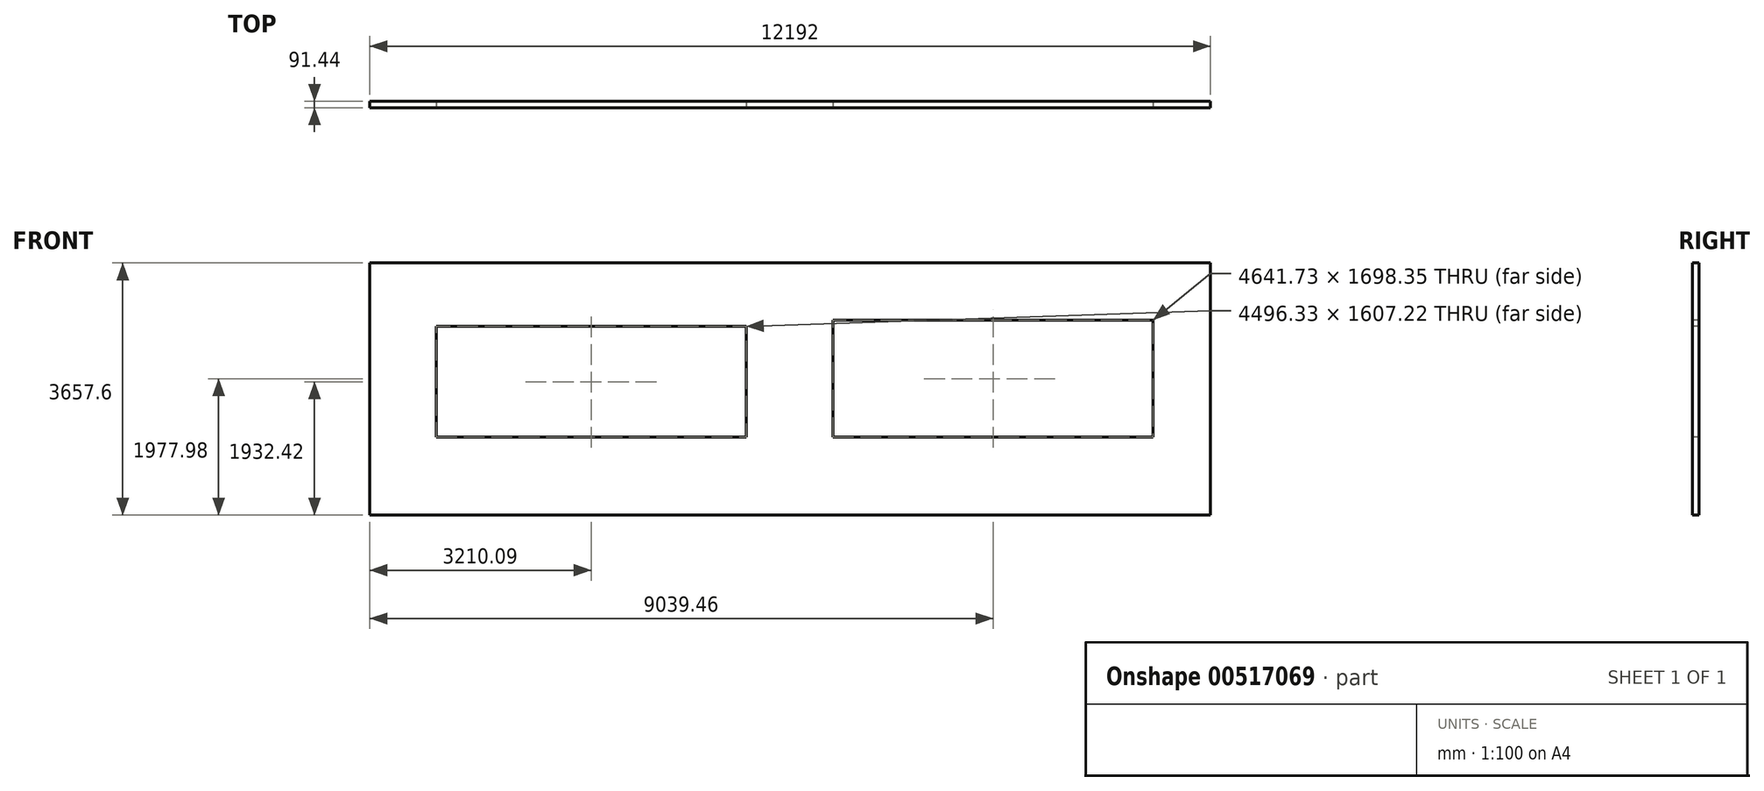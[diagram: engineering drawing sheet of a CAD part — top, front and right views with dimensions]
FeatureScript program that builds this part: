
annotation { "Feature Type Name" : "Feature", "Feature Type Description" : "" }
export const myFeature = defineFeature(function(context is Context, id is Id, definition is map)
    precondition{}
    {
        {
            var Q0;
            Q0=qCreatedBy(makeId("Top.planeOp"),FACE);
            var sketch = newSketch(context, id + "F0", { "sketchPlane" : qUnion([Q0])});
            skLineSegment(sketch, "E0.bottom", {"start": v(-5458.25, 883.27) * mm, "end": v(6733.75, 883.27) * mm});
            skLineSegment(sketch, "E0.top", {"start": v(-5458.25, 791.83) * mm, "end": v(6733.75, 791.83) * mm});
            skLineSegment(sketch, "E0.left", {"start": v(-5458.25, 883.27) * mm, "end": v(-5458.25, 791.83) * mm});
            skLineSegment(sketch, "E0.right", {"start": v(6733.75, 883.27) * mm, "end": v(6733.75, 791.83) * mm});
            skSolve(sketch);
        }
        {
            var Q0;
            Q0=makeQuery(id+"F0.imprint","IMPRINT",FACE,{"disambiguationData":[TD([[makeQuery(id+"F0.imprint","IMPRINT",EDGE,{"derivedFrom":sQuery(id+"F0.wireOp",EDGE,"E0.bottom")}),-1.0]])]});
            extrude(context, id + "F1", {"entities" : qUnion([Q0]), "depth" : 3657.6 * mm, "offsetDistance" : 30.48 * mm});
        }
        {
            var Q0;
            Q0=makeQuery(id+"F1.opExtrude","SWEPT_FACE",FACE,{"disambiguationData":[OSD([sQuery(id+"F0.wireOp",EDGE,"E0.top")])]});
            var sketch = newSketch(context, id + "F2", { "sketchPlane" : qUnion([Q0])});
            skLineSegment(sketch, "E1.bottom", {"start": v(-4496.33, 2736.03) * mm, "end": v(0, 2736.03) * mm});
            skLineSegment(sketch, "E1.top", {"start": v(-4496.33, 1128.8) * mm, "end": v(0, 1128.8) * mm});
            skLineSegment(sketch, "E1.left", {"start": v(-4496.33, 2736.03) * mm, "end": v(-4496.33, 1128.8) * mm});
            skLineSegment(sketch, "E1.right", {"start": v(0, 2736.03) * mm, "end": v(0, 1128.8) * mm});
            skLineSegment(sketch, "E2.bottom", {"start": v(5902.08, 2827.15) * mm, "end": v(1260.35, 2827.15) * mm});
            skLineSegment(sketch, "E2.top", {"start": v(5902.08, 1128.8) * mm, "end": v(1260.35, 1128.8) * mm});
            skLineSegment(sketch, "E2.left", {"start": v(5902.08, 2827.15) * mm, "end": v(5902.08, 1128.8) * mm});
            skLineSegment(sketch, "E2.right", {"start": v(1260.35, 2827.15) * mm, "end": v(1260.35, 1128.8) * mm});
            skSolve(sketch);
        }
        {
            var Q0;
            Q0 = qSketchRegion(id + "F2", true);
            extrude(context, id + "F3", {"entities" : qUnion([Q0]), "operationType" : NewBodyOperationType.REMOVE, "oppositeDirection" : true, "depth" : 6858 * mm, "offsetDistance" : 30.48 * mm});
        }
    });
